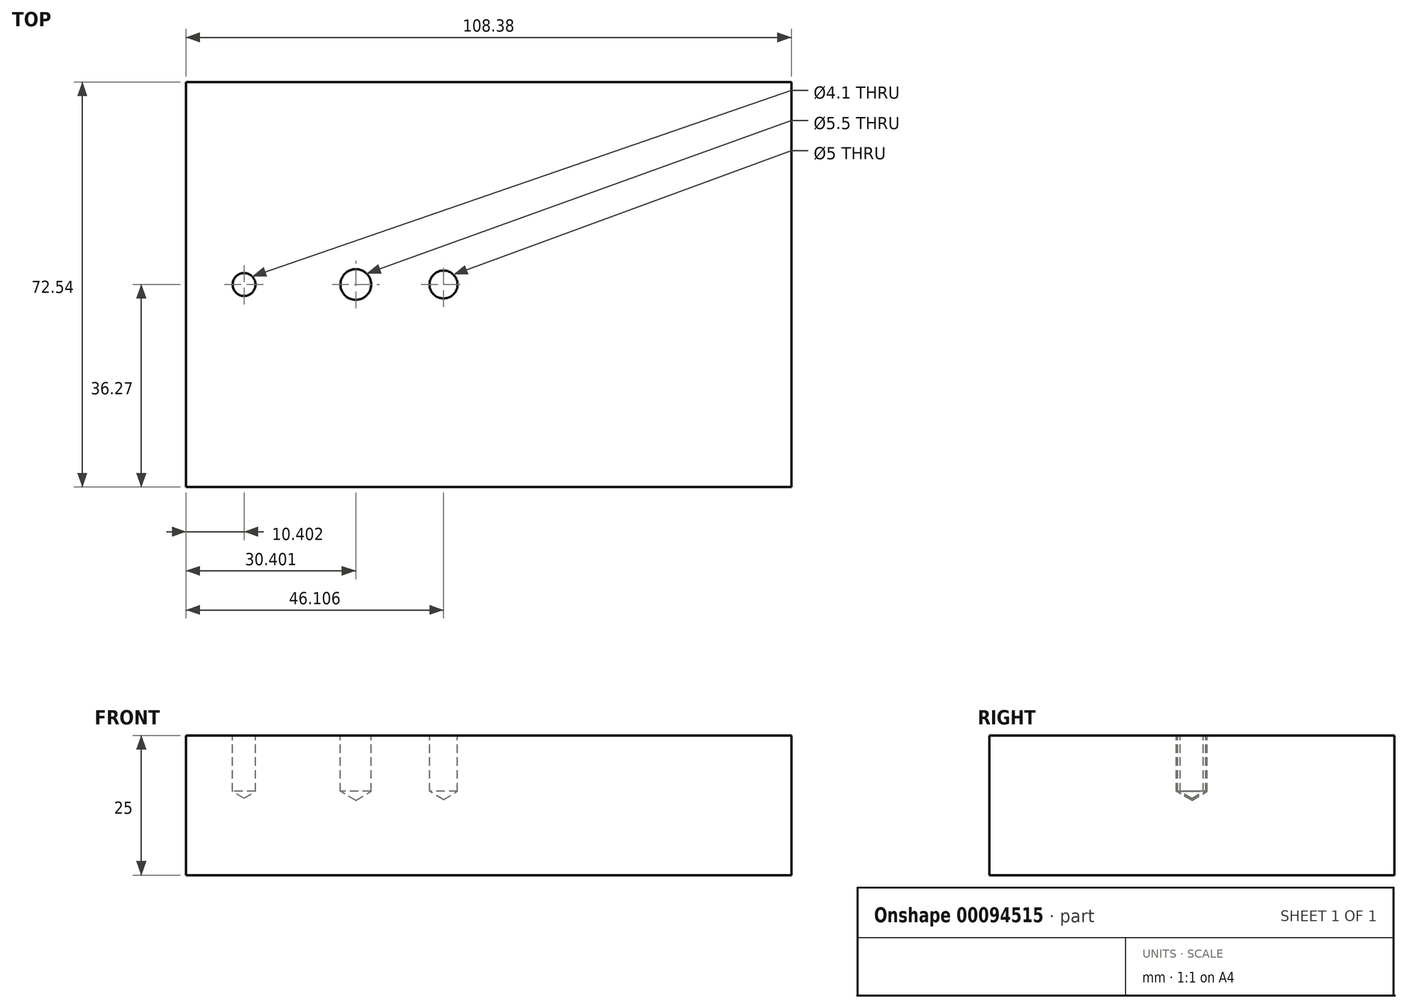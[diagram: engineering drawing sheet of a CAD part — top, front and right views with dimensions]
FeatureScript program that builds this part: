
annotation { "Feature Type Name" : "Feature", "Feature Type Description" : "" }
export const myFeature = defineFeature(function(context is Context, id is Id, definition is map)
    precondition{}
    {
        {
            var Q0;
            Q0=qCreatedBy(makeId("Top.planeOp"),FACE);
            var sketch = newSketch(context, id + "F0", { "sketchPlane" : qUnion([Q0])});
            skLineSegment(sketch, "E0.bottom", {"start": v(54.2, 36.27) * mm, "end": v(-54.2, 36.27) * mm});
            skLineSegment(sketch, "E0.top", {"start": v(54.2, -36.27) * mm, "end": v(-54.2, -36.27) * mm});
            skLineSegment(sketch, "E0.left", {"start": v(54.2, 36.27) * mm, "end": v(54.2, -36.27) * mm});
            skLineSegment(sketch, "E0.right", {"start": v(-54.2, 36.27) * mm, "end": v(-54.2, -36.27) * mm});
            skPoint(sketch, "E0.middle", {"position": v(0, 0) * mm});
            skSolve(sketch);
        }
        {
            var Q0;
            Q0=makeQuery(id+"F0.imprint","IMPRINT",FACE,{"disambiguationData":[TD([[makeQuery(id+"F0.imprint","IMPRINT",EDGE,{"derivedFrom":sQuery(id+"F0.wireOp",EDGE,"E0.bottom")}),1.0]])]});
            extrude(context, id + "F1", {"entities" : qUnion([Q0]), "depth" : 25 * mm});
        }
        {
            var Q0;
            Q0=makeQuery(id+"F1.opExtrude","CAP_FACE",FACE,{"disambiguationData":[OSD([sQuery(id+"F0.wireOp",EDGE,"E0.bottom"),sQuery(id+"F0.wireOp",EDGE,"E0.top"),sQuery(id+"F0.wireOp",EDGE,"E0.left"),sQuery(id+"F0.wireOp",EDGE,"E0.right")])],"isStart":false});
            var sketch = newSketch(context, id + "F2", { "sketchPlane" : qUnion([Q0])});
            skLineSegment(sketch, "E1", {"start": v(-54.2, 0) * mm, "end": v(54.2, 0) * mm});
            skPoint(sketch, "E2", {"position": v(-43.79, 0) * mm});
            skPoint(sketch, "E3", {"position": v(-23.79, 0) * mm});
            skPoint(sketch, "E4", {"position": v(-8.08, 0) * mm});
            skPoint(sketch, "E5", {"position": v(9.77, 0) * mm});
            skPoint(sketch, "E6", {"position": v(27.2, 0) * mm});
            skPoint(sketch, "E7", {"position": v(43.86, 0) * mm});
            skSolve(sketch);
        }
        {
            var Q0;
            Q0=sQuery(id+"F2.wireOp",VERTEX,"E2");
            var Q1;
            Q1=makeQuery(id+"F1.opExtrude","SWEPT_BODY",BODY,{"disambiguationData":[OSD([sQuery(id+"F0.wireOp",EDGE,"E0.bottom"),sQuery(id+"F0.wireOp",EDGE,"E0.top"),sQuery(id+"F0.wireOp",EDGE,"E0.left"),sQuery(id+"F0.wireOp",EDGE,"E0.right")])]});
            hole(context, id + "F3", {"style" : HoleStyle.SIMPLE, "endStyle" : HoleEndStyle.BLIND, "standardTappedOrClearance" : lookupTablePath({ "standard" : "ISO", "engagement" : "75%", "pitch" : "0.9 mm", "size" : "M5", "type" : "Tapped" }), "standardBlindInLast" : lookupTablePath({ "standard" : "ISO", "engagement" : "75%", "pitch" : "0.9 mm", "size" : "M5", "type" : "Tapped" }), "holeDiameter" : 4.1 * mm, "holeDepth" : 10 * mm, "locations" : qUnion([Q0]), "scope" : qUnion([Q1])});
        }
        {
            var Q0;
            Q0=sQuery(id+"F2.wireOp",VERTEX,"E3");
            var Q1;
            Q1=makeQuery(id+"F1.opExtrude","SWEPT_BODY",BODY,{"disambiguationData":[OSD([sQuery(id+"F0.wireOp",EDGE,"E0.bottom"),sQuery(id+"F0.wireOp",EDGE,"E0.top"),sQuery(id+"F0.wireOp",EDGE,"E0.left"),sQuery(id+"F0.wireOp",EDGE,"E0.right")])]});
            hole(context, id + "F4", {"style" : HoleStyle.SIMPLE, "endStyle" : HoleEndStyle.BLIND, "standardTappedOrClearance" : lookupTablePath({ "standard" : "ISO", "fit" : "Normal", "size" : "M5", "type" : "Clearance" }), "standardBlindInLast" : lookupTablePath({ "fit" : "Standard", "standard" : "ISO", "size" : "M5", "type" : "Clearance" }), "holeDiameter" : 5.5 * mm, "holeDepth" : 10 * mm, "locations" : qUnion([Q0]), "scope" : qUnion([Q1])});
        }
        {
            var Q0;
            Q0=sQuery(id+"F2.wireOp",VERTEX,"E4");
            var Q1;
            Q1=makeQuery(id+"F1.opExtrude","SWEPT_BODY",BODY,{"disambiguationData":[OSD([sQuery(id+"F0.wireOp",EDGE,"E0.bottom"),sQuery(id+"F0.wireOp",EDGE,"E0.top"),sQuery(id+"F0.wireOp",EDGE,"E0.left"),sQuery(id+"F0.wireOp",EDGE,"E0.right")])]});
            hole(context, id + "F5", {"style" : HoleStyle.SIMPLE, "endStyle" : HoleEndStyle.BLIND, "standardTappedOrClearance" : lookupTablePath({ "standard" : "ISO", "size" : "5", "type" : "Drilled" }), "standardBlindInLast" : lookupTablePath({ "standard" : "ISO", "size" : "5", "type" : "Drilled" }), "holeDiameter" : 5 * mm, "holeDepth" : 10 * mm, "locations" : qUnion([Q0]), "scope" : qUnion([Q1])});
        }
    });
